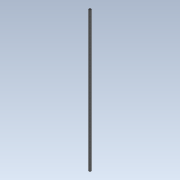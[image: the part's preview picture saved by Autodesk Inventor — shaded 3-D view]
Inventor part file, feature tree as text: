
AUTODESK INVENTOR PART (.ipt)
format: ipt  version: 2022 (Build 260153000, 153)  size: 74,752 bytes
history: native  units: mm
features: extrude x1, thread x1, sketch x1
ambient origin geometry x8: Origin, YZ Plane, XZ Plane, XY Plane, X Axis, Y Axis, Z Axis, Center Point
bodies: Solid1 (feature_tree)
feature tree (3):
  extrude  "Extrusion1"  Depth=378.0mm TaperAngle=0.0deg
  thread  "Thread1"  [1 undecoded]
  sketch  "Sketch1"  dims[d0=6.0mm d1=378.0mm d2=0.0mm d3=400.0mm d4=0.0mm]
note: 1 required parameter value undecoded (feature->parameter linkage not recoverable at this tier; creation-order binding heuristic only, values carry confidence <= 0.55)
